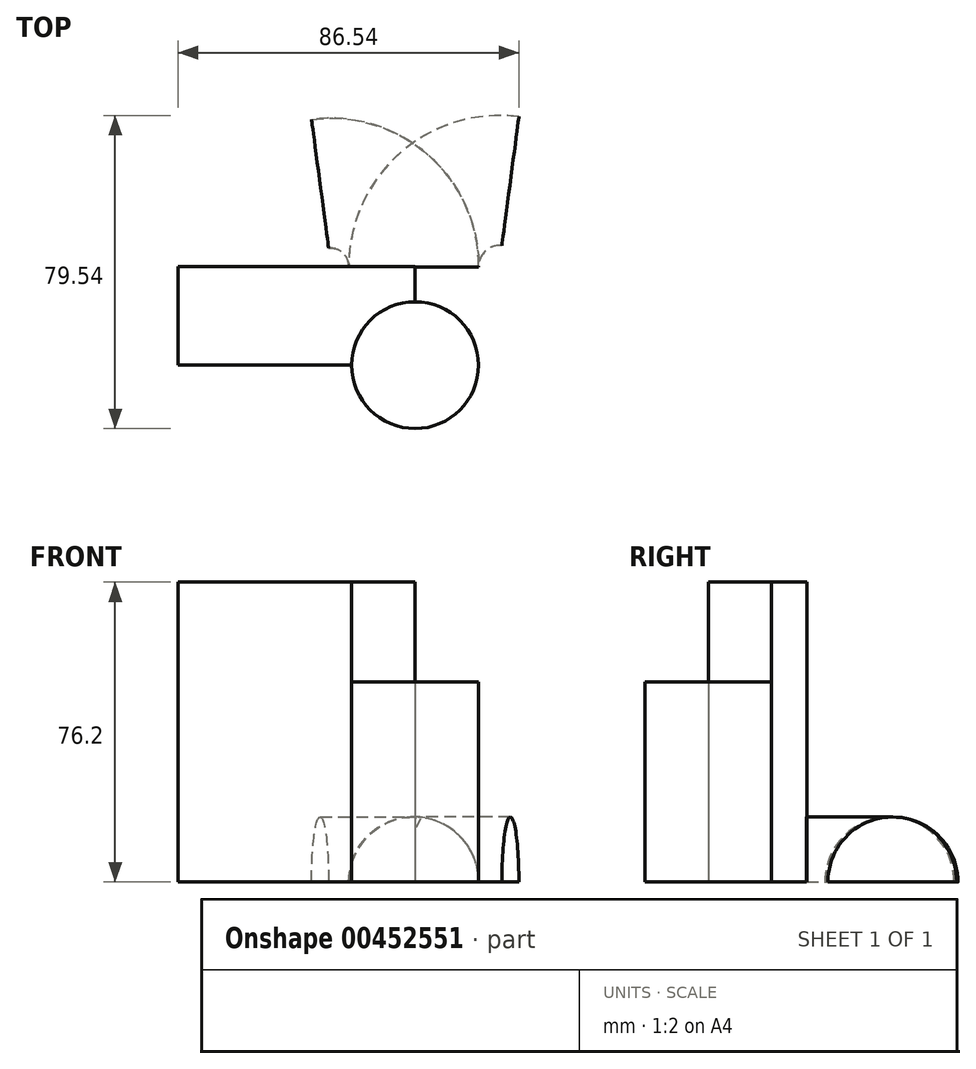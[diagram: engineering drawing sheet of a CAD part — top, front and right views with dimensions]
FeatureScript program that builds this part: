
annotation { "Feature Type Name" : "Feature", "Feature Type Description" : "" }
export const myFeature = defineFeature(function(context is Context, id is Id, definition is map)
    precondition{}
    {
        {
            var Q0;
            Q0=qCreatedBy(makeId("Top.planeOp"),FACE);
            var sketch = newSketch(context, id + "F0", { "sketchPlane" : qUnion([Q0])});
            skLineSegment(sketch, "E0.bottom", {"start": v(-30.68, 0.13) * mm, "end": v(29.48, 0.13) * mm});
            skLineSegment(sketch, "E0.top", {"start": v(-30.68, -24.97) * mm, "end": v(29.48, -24.97) * mm});
            skLineSegment(sketch, "E0.left", {"start": v(-30.68, 0.13) * mm, "end": v(-30.68, -24.97) * mm});
            skLineSegment(sketch, "E0.right", {"start": v(29.48, 0.13) * mm, "end": v(29.48, -24.97) * mm});
            skCircle(sketch, "E1", {"center": v(29.48, -24.97) * mm, "radius": 16.1 * mm});
            skArc(sketch, "E2", {"start": v(53.78, 21.44) * mm, "mid": v(36.8, 16.29) * mm, "end": v(29.48, 0.13) * mm});
            skArc(sketch, "E3.MirrorCS", {"start": v(5.17, 21.44) * mm, "mid": v(22.15, 16.29) * mm, "end": v(29.48, 0.13) * mm});
            skSolve(sketch);
        }
        {
            var Q0;
            Q0=qCreatedBy(makeId("Front.planeOp"),FACE);
            var sketch = newSketch(context, id + "F1", { "sketchPlane" : qUnion([Q0])});
            skArc(sketch, "E4", {"start": v(45.65, 0) * mm, "mid": v(29.14, 16.5) * mm, "end": v(12.63, 0) * mm});
            skLineSegment(sketch, "E5", {"start": v(29.14, 0) * mm, "end": v(45.65, 0) * mm});
            skLineSegment(sketch, "E6", {"start": v(29.14, 0) * mm, "end": v(12.63, 0) * mm});
            skSolve(sketch);
        }
        {
            var Q0;
            {var subQ1=sQuery(id+"F0.wireOp",EDGE,"E0.bottom");Q0=makeQuery(id+"F0.imprint","IMPRINT",FACE,{"disambiguationData":[TD([[makeQuery(id+"F0.imprint","IMPRINT",EDGE,{"derivedFrom":subQ1}),-1.0]])]});}
            extrude(context, id + "F2", {"entities" : qUnion([Q0]), "depth" : 76.2 * mm});
        }
        {
            var Q0;
            {var subQ0=sQuery(id+"F0.wireOp",EDGE,"E0.right");var subQ1=sQuery(id+"F0.wireOp",EDGE,"E0.top");var subQ2=makeQuery(id+"F0.imprint","INTERSECT",VERTEX,{"derivedFrom":[subQ1,subQ0]});Q0=makeQuery(id+"F0.imprint","IMPRINT",FACE,{"disambiguationData":[TD([[makeQuery(id+"F0.imprint","IMPRINT",EDGE,{"disambiguationData":[TD([[subQ2,1.0]])],"derivedFrom":subQ1}),1.0]])]});}
            var Q1;
            {var subQ0=sQuery(id+"F0.wireOp",EDGE,"E0.right");var subQ1=sQuery(id+"F0.wireOp",EDGE,"E0.top");var subQ2=makeQuery(id+"F0.imprint","INTERSECT",VERTEX,{"derivedFrom":[subQ1,subQ0]});Q1=makeQuery(id+"F0.imprint","IMPRINT",FACE,{"disambiguationData":[TD([[makeQuery(id+"F0.imprint","IMPRINT",EDGE,{"disambiguationData":[TD([[subQ2,1.0]])],"derivedFrom":subQ1}),-1.0]])]});}
            extrude(context, id + "F3", {"entities" : qUnion([Q0, Q1]), "operationType" : NewBodyOperationType.ADD, "depth" : 50.8 * mm});
        }
        {
            var Q0;
            Q0=makeQuery(id+"F1.imprint","IMPRINT",FACE,{"disambiguationData":[TD([[makeQuery(id+"F1.imprint","IMPRINT",EDGE,{"derivedFrom":sQuery(id+"F1.wireOp",EDGE,"E4")}),1.0]])]});
            var Q1;
            Q1=sQuery(id+"F0.wireOp",EDGE,"E2");
            var Q2;
            Q2=sQuery(id+"F0.wireOp",EDGE,"E3.MirrorCS");
            var Q3;
            Q3=sQuery(id+"F0.wireOp",EDGE,"E2");
            sweep(context, id + "F4", {"profiles" : qUnion([Q0]), "surfaceProfiles" : qUnion([Q1, Q2]), "path" : qUnion([Q3])});
        }
        {
            var Q0;
            Q0=makeQuery(id+"F4.opSweep","CAP_FACE",FACE,{"disambiguationData":[OSD([sQuery(id+"F0.wireOp",VERTEX,"E2.end"),sQuery(id+"F1.wireOp",EDGE,"E4"),sQuery(id+"F1.wireOp",EDGE,"E5"),sQuery(id+"F1.wireOp",EDGE,"E6")])],"isStart":true});
            var Q1;
            Q1=sQuery(id+"F0.wireOp",EDGE,"E3.MirrorCS");
            sweep(context, id + "F5", {"profiles" : qUnion([Q0]), "path" : qUnion([Q1])});
        }
    });
